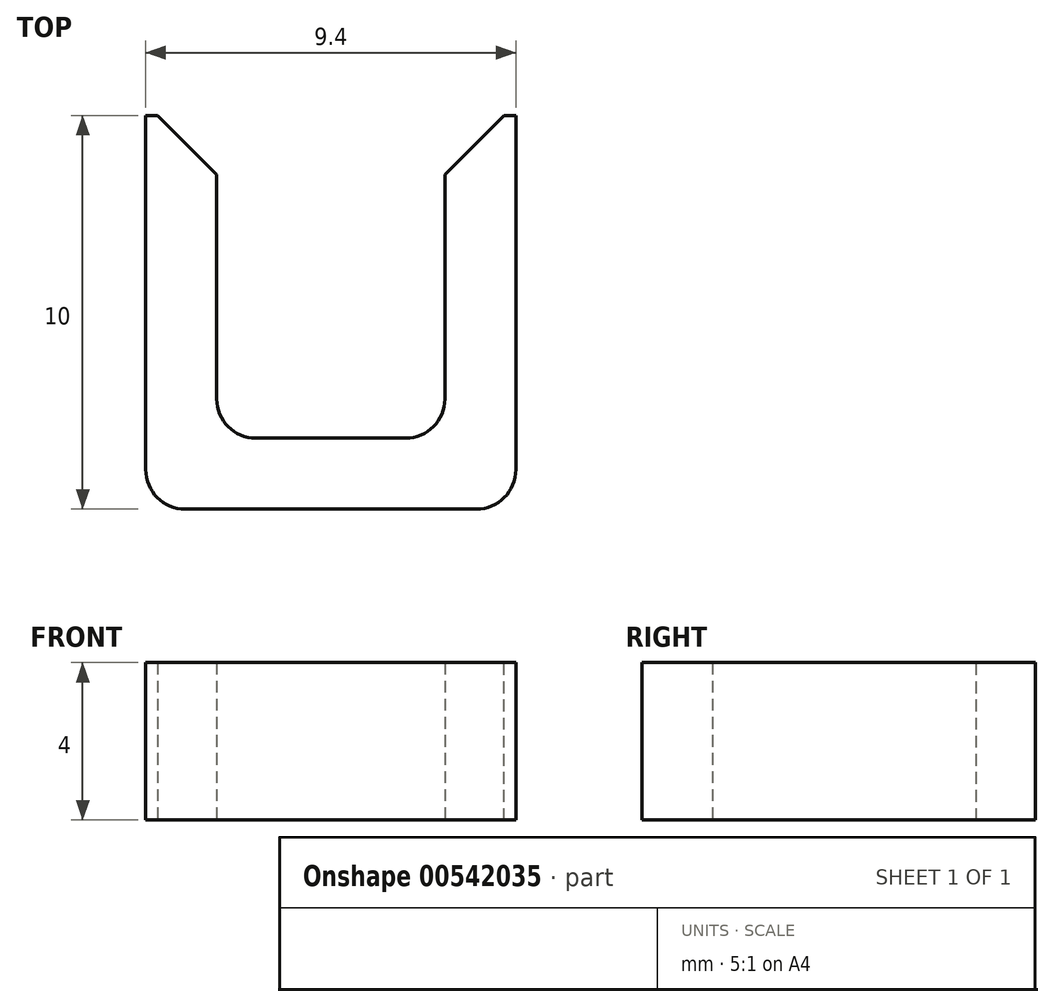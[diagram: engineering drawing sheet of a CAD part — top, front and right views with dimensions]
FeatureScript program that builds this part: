
annotation { "Feature Type Name" : "Feature", "Feature Type Description" : "" }
export const myFeature = defineFeature(function(context is Context, id is Id, definition is map)
    precondition{}
    {
        {
            var Q0;
            Q0=qCreatedBy(makeId("Top.planeOp"),FACE);
            var sketch = newSketch(context, id + "F0", { "sketchPlane" : qUnion([Q0])});
            skLineSegment(sketch, "E0", {"start": v(-2.9, 8.2) * mm, "end": v(-2.9, 0) * mm});
            skLineSegment(sketch, "E1", {"start": v(-2.9, 0) * mm, "end": v(2.9, 0) * mm});
            skLineSegment(sketch, "E2", {"start": v(2.9, 0) * mm, "end": v(2.9, 8.2) * mm});
            skLineSegment(sketch, "E3", {"start": v(2.9, 8.2) * mm, "end": v(4.7, 8.2) * mm});
            skLineSegment(sketch, "E4", {"start": v(4.7, 8.2) * mm, "end": v(4.7, -1.8) * mm});
            skLineSegment(sketch, "E5", {"start": v(4.7, -1.8) * mm, "end": v(-4.7, -1.8) * mm});
            skLineSegment(sketch, "E6", {"start": v(-4.7, -1.8) * mm, "end": v(-4.7, 8.2) * mm});
            skLineSegment(sketch, "E7", {"start": v(-4.7, 8.2) * mm, "end": v(-2.9, 8.2) * mm});
            skLineSegment(sketch, "E8", {"start": v(0, 0) * mm, "end": v(0, -1.8) * mm, "construction": true});
            skSolve(sketch);
        }
        {
            var Q0;
            Q0 = qSketchRegion(id + "F0", true);
            extrude(context, id + "F1", {"entities" : qUnion([Q0]), "depth" : 4 * mm, "offsetDistance" : 25 * mm});
        }
        {
            var Q0;
            Q0=makeQuery(id+"F1.opExtrude","SWEPT_EDGE",EDGE,{"disambiguationData":[OSD([sQuery(id+"F0.wireOp",EDGE,"E0"),sQuery(id+"F0.wireOp",EDGE,"E7")])]});
            var Q1;
            Q1=makeQuery(id+"F1.opExtrude","SWEPT_EDGE",EDGE,{"disambiguationData":[OSD([sQuery(id+"F0.wireOp",EDGE,"E2"),sQuery(id+"F0.wireOp",EDGE,"E3")])]});
            chamfer(context, id + "F2", {"entities" : qUnion([Q0, Q1]), "width" : 1.5 * mm, "tangentPropagation" : true});
        }
        {
            var Q0;
            Q0=makeQuery(id+"F1.opExtrude","SWEPT_EDGE",EDGE,{"disambiguationData":[OSD([sQuery(id+"F0.wireOp",EDGE,"E0"),sQuery(id+"F0.wireOp",EDGE,"E1")])]});
            var Q1;
            Q1=makeQuery(id+"F1.opExtrude","SWEPT_EDGE",EDGE,{"disambiguationData":[OSD([sQuery(id+"F0.wireOp",EDGE,"E1"),sQuery(id+"F0.wireOp",EDGE,"E2")])]});
            var Q2;
            Q2=makeQuery(id+"F1.opExtrude","SWEPT_EDGE",EDGE,{"disambiguationData":[OSD([sQuery(id+"F0.wireOp",EDGE,"E5"),sQuery(id+"F0.wireOp",EDGE,"E6")])]});
            var Q3;
            Q3=makeQuery(id+"F1.opExtrude","SWEPT_EDGE",EDGE,{"disambiguationData":[OSD([sQuery(id+"F0.wireOp",EDGE,"E4"),sQuery(id+"F0.wireOp",EDGE,"E5")])]});
            fillet(context, id + "F3", {"entities" : qUnion([Q0, Q1, Q2, Q3]), "radius" : 1 * mm, "tangentPropagation" : true, "allowEdgeOverflow" : false});
        }
    });
